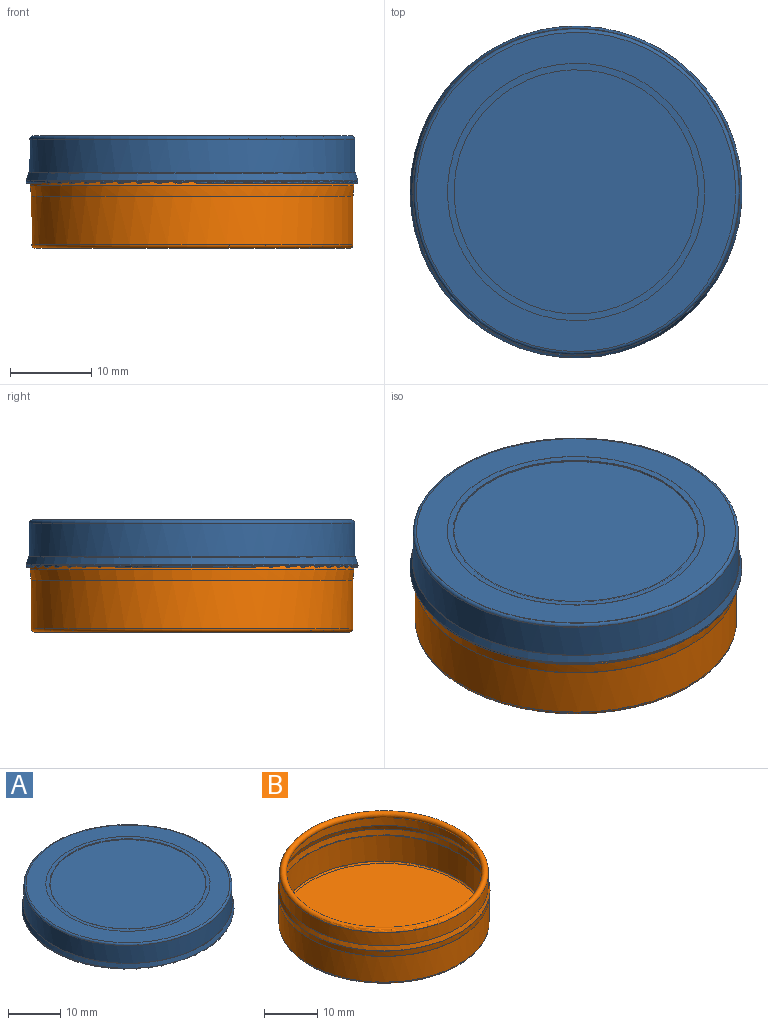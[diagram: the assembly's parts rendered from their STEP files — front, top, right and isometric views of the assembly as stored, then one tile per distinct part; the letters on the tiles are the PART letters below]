
ASSEMBLY  parts=2 mates=1
PART A: 19 faces, bbox 44.2x44.2x5.9 mm
  f0: cylinder r=20mm len=40mm, axis (0,0,-1), area 653.5mm2, adj f2,f3
  f1: plane 39.2x39.2mm, normal (0,0,1), area 422.6mm2, adj f3,f6
  f2: plane 40x40mm, normal (0,0,-1), area 0mm2, adj f0,f12
  f3: torus R=19.6mm, axis (0,0,1), area 78.4mm2, adj f0,f1
  f4: cylinder r=15mm len=30mm, axis (0,0,1), area 17.9mm2, adj f5,f6
  f5: plane 30x30mm, normal (0,0,1), area 706.9mm2, adj f4
  f6: cone r=15mm half-angle=89.3deg, axis (0,0,1), area 77.4mm2, adj f1,f4
  f7: cone r=20.29mm half-angle=16.3deg, axis (0,0,-1), area 129.1mm2, adj f8,f12
  f8: cone r=20.01mm half-angle=73.7deg, axis (0,0,1), area 12.6mm2, adj f7,f9
  f9: cone r=20.1mm half-angle=16.3deg, axis (0,0,-1), area 129.7mm2, adj f8,f10
  f10: torus R=20.15mm, axis (0,0,-1), area 108.6mm2, adj f9,f11
  f11: plane 39.8x39.8mm, normal (0,0,1), area 0mm2, adj f10,f18
  f12: torus R=20.15mm, axis (0,0,-1), area 65.1mm2, adj f2,f7
  f13: plane 30.2x30.2mm, normal (0,0,-1), area 716.3mm2, adj f14
  f14: cylinder r=15.1mm len=30.2mm, axis (0,0,1), area 18.1mm2, adj f13,f15
  f15: cone r=15mm half-angle=89.3deg, axis (0,0,1), area 68mm2, adj f14,f16
  f16: plane 39.2x39.2mm, normal (0,0,-1), area 422.5mm2, adj f15,f17
  f17: torus R=19.6mm, axis (0,0,1), area 58.6mm2, adj f16,f18
  f18: cylinder r=19.9mm len=39.8mm, axis (0,0,-1), area 650.2mm2, adj f11,f17
PART B: 19 faces, bbox 42.8x42.8x12.3 mm
  f0: cylinder r=19.75mm len=39.5mm, axis (0,0,-1), area 741.5mm2, adj f2,f7
  f1: plane 38.7x38.7mm, normal (0,0,-1), area 1176.3mm2, adj f7
  f2: plane 39.5x39.5mm, normal (0,0,1), area 0mm2, adj f0,f4
  f3: cone r=19.9mm half-angle=16.7deg, axis (0,0,-1), area 129.6mm2, adj f4,f6
  f4: cone r=19.75mm half-angle=6.6deg, axis (0,0,1), area 163mm2, adj f2,f3
  f5: plane 39.2x39.2mm, normal (0,0,1), area 0.1mm2, adj f6,f11
  f6: cylinder r=19.6mm len=39.2mm, axis (0,0,1), area 369.5mm2, adj f3,f5
  f7: torus R=19.35mm, axis (0,0,1), area 77.4mm2, adj f0,f1
  f8: plane 39x39mm, normal (0,0,-1), area 0.1mm2, adj f9,f18
  f9: torus R=18.95mm, axis (0,0,-1), area 348.8mm2, adj f8,f10
  f10: cone r=19.34mm half-angle=36.5deg, axis (0,0,-1), area 12.1mm2, adj f9,f11
  f11: torus R=18.95mm, axis (0,0,-1), area 411.8mm2, adj f5,f10
  f12: plane 38.7x38.7mm, normal (0,0,1), area 1176.3mm2, adj f13
  f13: torus R=19.35mm, axis (0,0,1), area 57.9mm2, adj f12,f14
  f14: cylinder r=19.65mm len=39.3mm, axis (0,0,-1), area 725.4mm2, adj f13,f15
  f15: plane 39.3x39.3mm, normal (0,0,-1), area 1.5mm2, adj f14,f16
  f16: cone r=19.65mm half-angle=6.6deg, axis (0,0,1), area 173.5mm2, adj f15,f17
  f17: cone r=19.8mm half-angle=16.7deg, axis (0,0,-1), area 126.4mm2, adj f16,f18
  f18: cylinder r=19.5mm len=39mm, axis (0,0,1), area 367.6mm2, adj f8,f17
PLACE A t=(0.01,-0.09,2.23)mm
PLACE B t=(0.01,-0.09,-5.95)mm
MATE cylindrical A.f0 <-> B.f0  axis (0,0,-1) through (0.01,-0.09,2.23)mm
